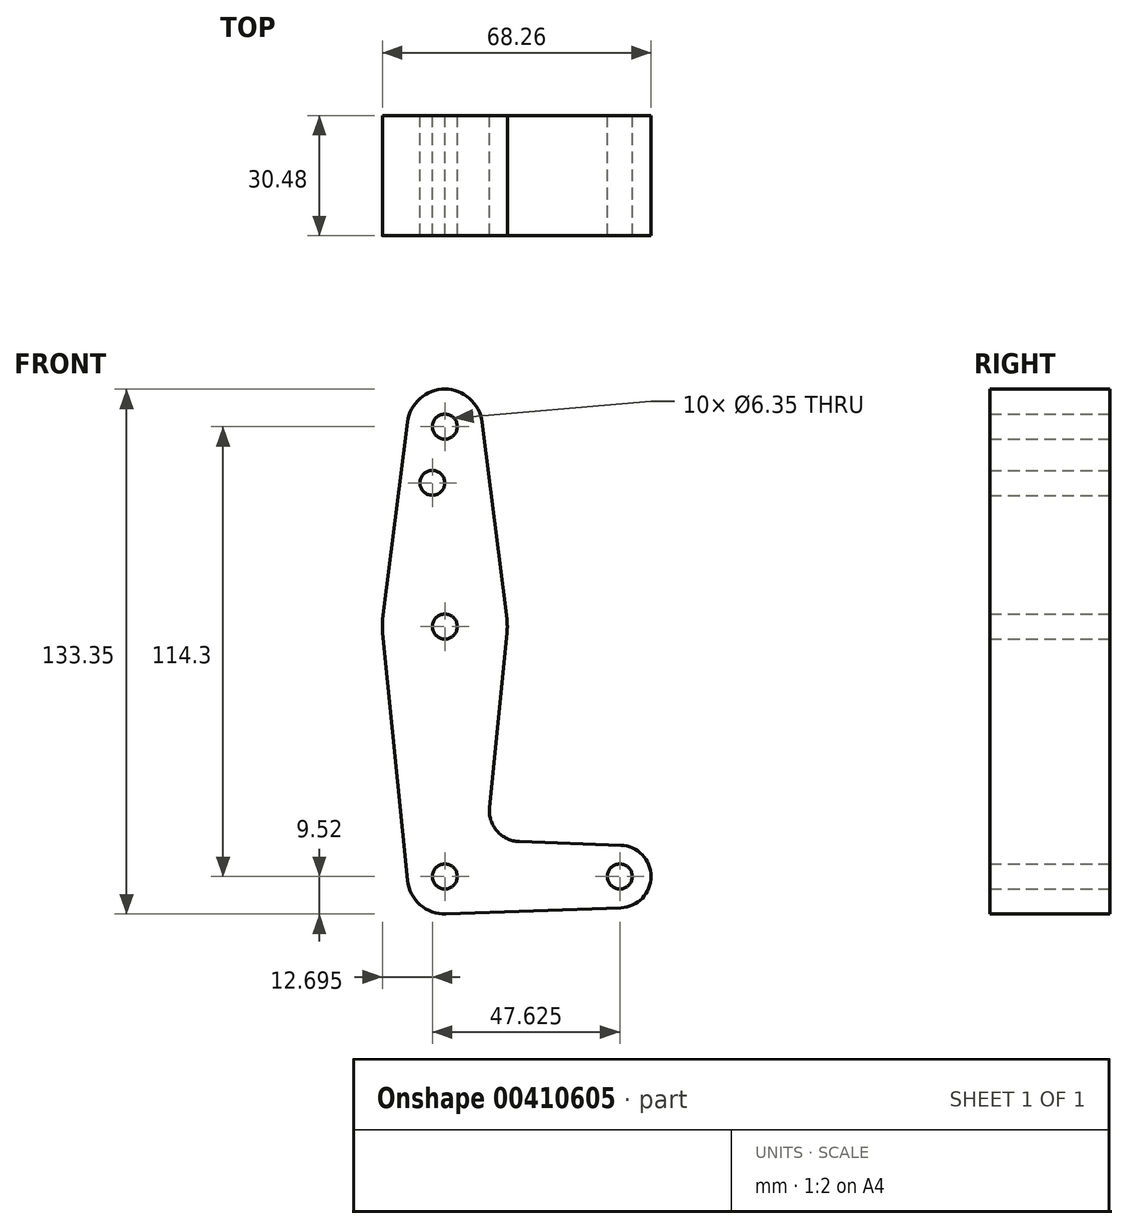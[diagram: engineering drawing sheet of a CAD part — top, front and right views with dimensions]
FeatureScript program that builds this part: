
annotation { "Feature Type Name" : "Feature", "Feature Type Description" : "" }
export const myFeature = defineFeature(function(context is Context, id is Id, definition is map)
    precondition{}
    {
        {
            var Q0;
            Q0=qCreatedBy(makeId("Front.planeOp"),FACE);
            var sketch = newSketch(context, id + "F0", { "sketchPlane" : qUnion([Q0])});
            skLineSegment(sketch, "E0", {"start": v(0, 114.3) * mm, "end": v(0, 0) * mm, "construction": true});
            skLineSegment(sketch, "E1", {"start": v(44.45, 0) * mm, "end": v(0, 0) * mm, "construction": true});
            skCircle(sketch, "E2", {"center": v(0, 114.3) * mm, "radius": 9.53 * mm});
            skCircle(sketch, "E3", {"center": v(0, 0) * mm, "radius": 9.53 * mm});
            skCircle(sketch, "E4", {"center": v(44.45, 0) * mm, "radius": 7.94 * mm});
            skCircle(sketch, "E5", {"center": v(0, 63.5) * mm, "radius": 15.88 * mm});
            skLineSegment(sketch, "E6", {"start": v(-9.45, 115.5) * mm, "end": v(-15.75, 65.48) * mm});
            skLineSegment(sketch, "E7", {"start": v(-15.8, 61.91) * mm, "end": v(-9.48, -0.95) * mm});
            skLineSegment(sketch, "E8", {"start": v(11.34, 17.6) * mm, "end": v(15.8, 61.91) * mm});
            skLineSegment(sketch, "E9", {"start": v(15.75, 65.48) * mm, "end": v(9.45, 115.5) * mm});
            skLineSegment(sketch, "E10", {"start": v(18.97, 8.85) * mm, "end": v(44.73, 7.93) * mm});
            skLineSegment(sketch, "E11", {"start": v(0.34, -9.52) * mm, "end": v(44.73, -7.93) * mm});
            skCircle(sketch, "E12", {"center": v(0, 114.3) * mm, "radius": 3.18 * mm});
            skCircle(sketch, "E13", {"center": v(0, 63.5) * mm, "radius": 3.18 * mm});
            skCircle(sketch, "E14", {"center": v(0, 0) * mm, "radius": 3.18 * mm});
            skCircle(sketch, "E15", {"center": v(44.45, 0) * mm, "radius": 3.18 * mm});
            skCircle(sketch, "E16", {"center": v(-3.18, 100.03) * mm, "radius": 3.18 * mm});
            skArc(sketch, "E17.filletArc", {"start": v(11.34, 17.6) * mm, "mid": v(13.26, 11.57) * mm, "end": v(18.97, 8.85) * mm});
            skSolve(sketch);
        }
        {
            var Q0;
            Q0 = qSketchRegion(id + "F0", true);
            extrude(context, id + "F1", {"entities" : qUnion([Q0]), "depth" : 30.48 * mm});
        }
    });
